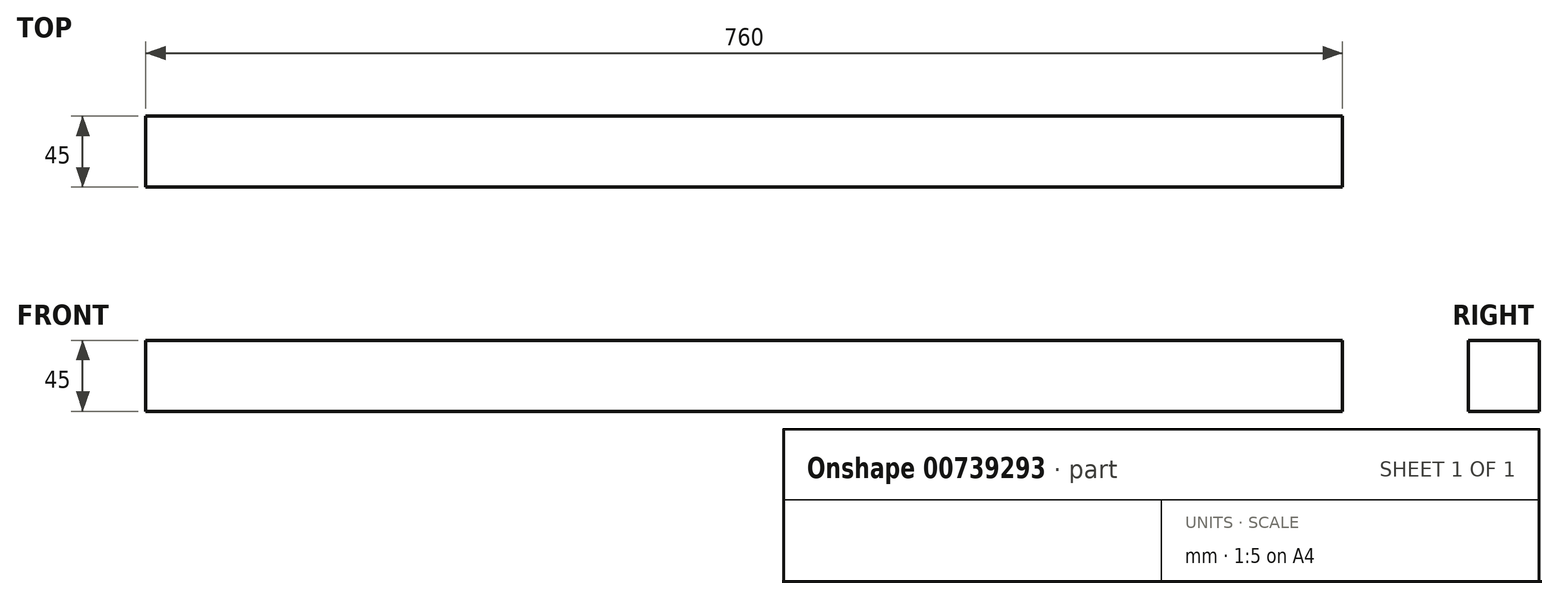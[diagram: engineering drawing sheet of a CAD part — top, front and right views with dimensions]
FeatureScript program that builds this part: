
annotation { "Feature Type Name" : "Feature", "Feature Type Description" : "" }
export const myFeature = defineFeature(function(context is Context, id is Id, definition is map)
    precondition{}
    {
        {
            var Q0;
            Q0=qCreatedBy(makeId("Right.planeOp"),FACE);
            var sketch = newSketch(context, id + "F0", { "sketchPlane" : qUnion([Q0])});
            skLineSegment(sketch, "E0", {"start": v(0, 45) * mm, "end": v(0, 0) * mm});
            skLineSegment(sketch, "E1", {"start": v(0, 0) * mm, "end": v(45, 0) * mm});
            skLineSegment(sketch, "E2", {"start": v(45, 0) * mm, "end": v(45, 45) * mm});
            skLineSegment(sketch, "E3", {"start": v(45, 45) * mm, "end": v(0, 45) * mm});
            skSolve(sketch);
        }
        {
            var Q0;
            Q0=makeQuery(id+"F0.imprint","IMPRINT",FACE,{"disambiguationData":[TD([[makeQuery(id+"F0.imprint","IMPRINT",EDGE,{"derivedFrom":sQuery(id+"F0.wireOp",EDGE,"E0")}),1.0]])]});
            extrude(context, id + "F1", {"entities" : qUnion([Q0]), "depth" : 760 * mm, "offsetDistance" : 25 * mm});
        }
    });
